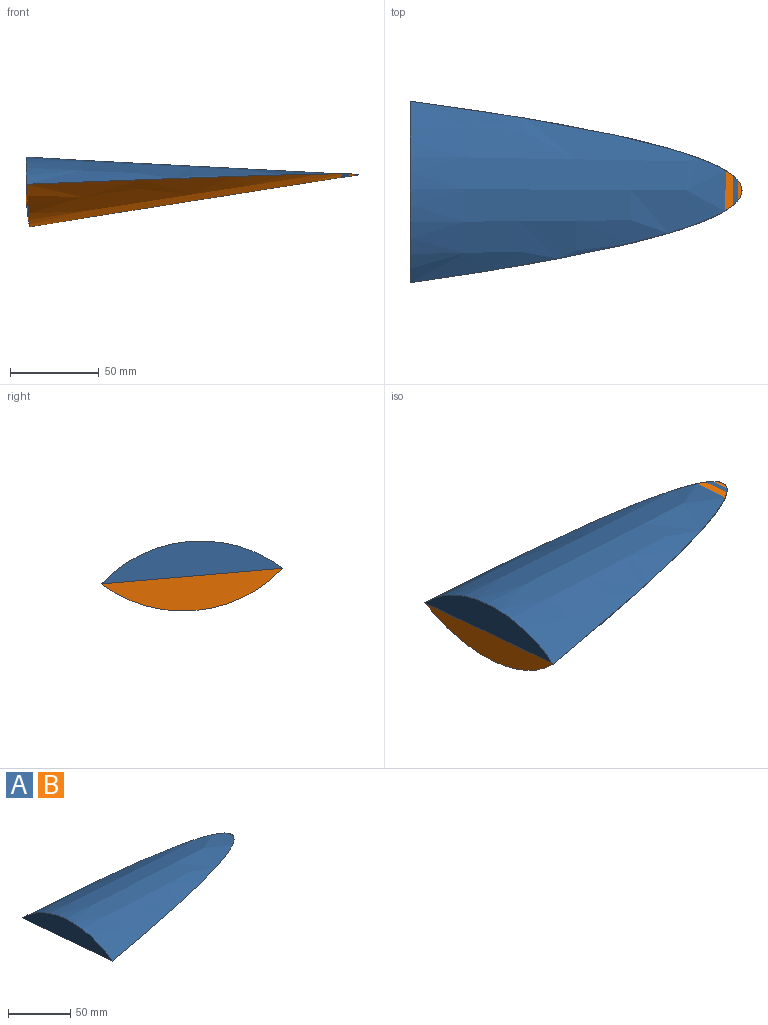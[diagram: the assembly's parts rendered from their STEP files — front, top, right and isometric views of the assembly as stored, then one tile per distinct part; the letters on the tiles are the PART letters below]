
ASSEMBLY  parts=2 mates=1
PART A: 3 faces, bbox 187x102.2x30.9 mm
  f0: plane 186.99x102.25mm, normal (0.05,-0.09,-0.99), area 12800.2mm2, adj f1,f2
  f1: cone r=76.96mm half-angle=3deg, axis (-1,0,0), area 13533.6mm2, adj f0,f2
  f2: plane 102.24x24.22mm, normal (-1,0,0), area 1379mm2, adj f0,f1
PART B: same geometry as A
PLACE A t=(-3.41,103.44,158.12)mm
PLACE B rot(axis=(-1,0,-0.05),180deg) t=(15.05,-296.98,-161.02)mm
MATE fastened B.f0 <-> A.f0  axis (-0.05,0.09,0.99) through (71.39,-96.47,1.97)mm
